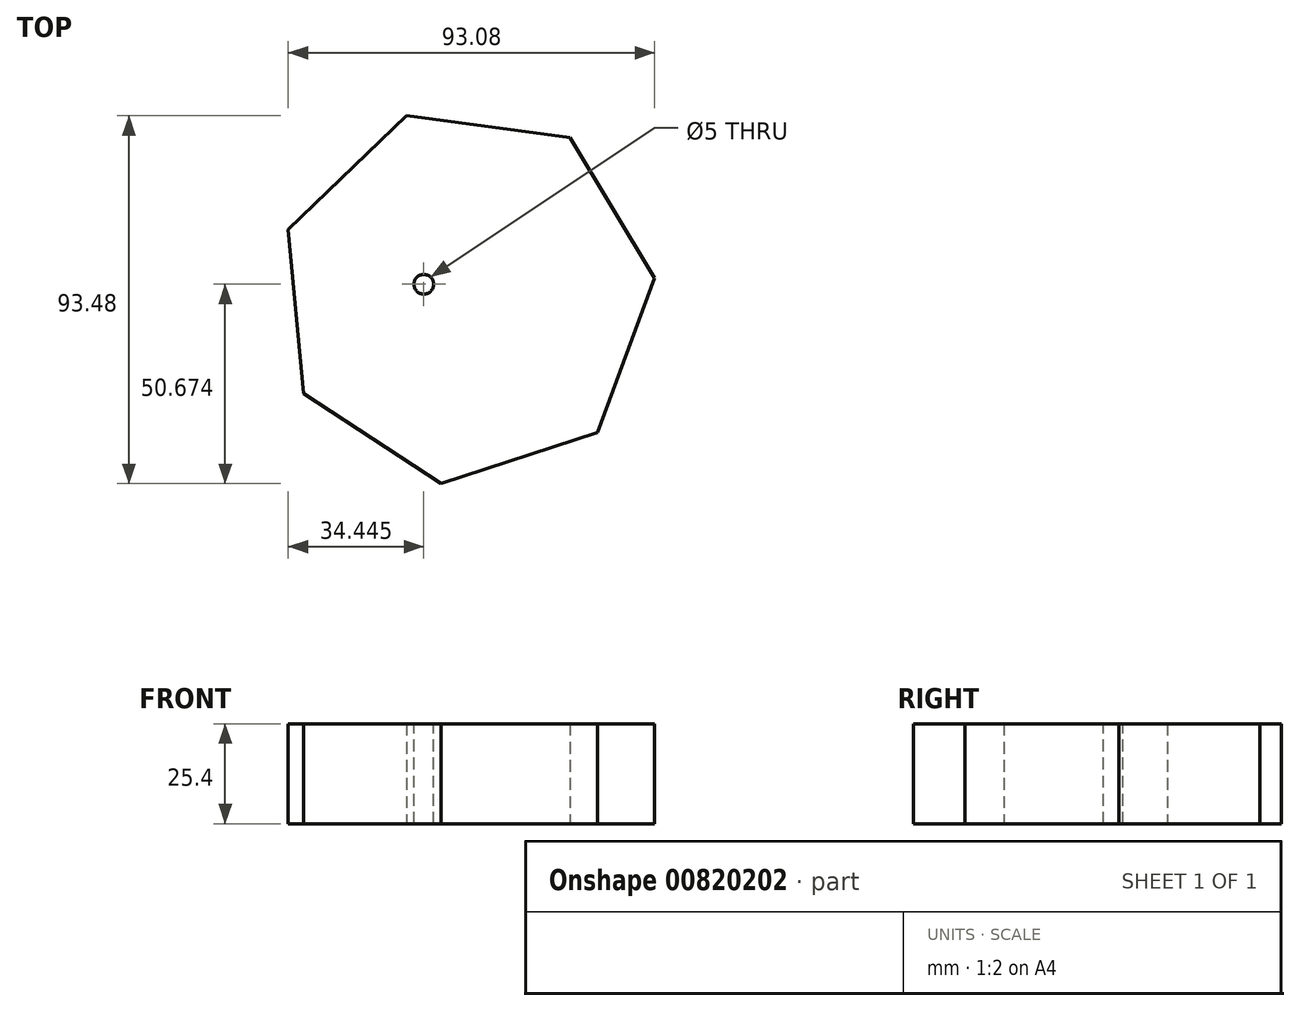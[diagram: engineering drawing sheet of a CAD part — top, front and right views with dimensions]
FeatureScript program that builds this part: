
annotation { "Feature Type Name" : "Feature", "Feature Type Description" : "" }
export const myFeature = defineFeature(function(context is Context, id is Id, definition is map)
    precondition{}
    {
        {
            var Q0;
            Q0=qCreatedBy(makeId("Top.planeOp"),FACE);
            var sketch = newSketch(context, id + "F0", { "sketchPlane" : qUnion([Q0])});
            skCircle(sketch, "E0.cCircle", {"center": v(15.97, -34.84) * mm, "radius": 43.38 * mm, "construction": true});
            skLineSegment(sketch, "E0.0", {"start": v(49.35, -69.54) * mm, "end": v(9.65, -82.57) * mm});
            skLineSegment(sketch, "E0.1", {"start": v(9.65, -82.57) * mm, "end": v(-25.29, -59.66) * mm});
            skLineSegment(sketch, "E0.2", {"start": v(-25.29, -59.66) * mm, "end": v(-29.16, -18.05) * mm});
            skLineSegment(sketch, "E0.3", {"start": v(-29.16, -18.05) * mm, "end": v(0.96, 10.91) * mm});
            skLineSegment(sketch, "E0.4", {"start": v(0.96, 10.91) * mm, "end": v(42.38, 5.43) * mm});
            skLineSegment(sketch, "E0.5", {"start": v(42.38, 5.43) * mm, "end": v(63.92, -30.38) * mm});
            skLineSegment(sketch, "E0.6", {"start": v(63.92, -30.38) * mm, "end": v(49.35, -69.54) * mm});
            skPoint(sketch, "E0.0.midPoint", {"position": v(29.5, -76.06) * mm});
            skSolve(sketch);
        }
        {
            var Q0;
            Q0=makeQuery(id+"F0.imprint","IMPRINT",FACE,{"disambiguationData":[TD([[makeQuery(id+"F0.imprint","IMPRINT",EDGE,{"derivedFrom":sQuery(id+"F0.wireOp",EDGE,"E0.0")}),-1.0]])]});
            extrude(context, id + "F1", {"entities" : qUnion([Q0]), "depth" : 25.4 * mm, "offsetDistance" : 25.4 * mm});
        }
        {
            var Q0;
            Q0=makeQuery(id+"F1.opExtrude","CAP_FACE",FACE,{"disambiguationData":[OSD([sQuery(id+"F0.wireOp",EDGE,"E0.0"),sQuery(id+"F0.wireOp",EDGE,"E0.1"),sQuery(id+"F0.wireOp",EDGE,"E0.2"),sQuery(id+"F0.wireOp",EDGE,"E0.3"),sQuery(id+"F0.wireOp",EDGE,"E0.4"),sQuery(id+"F0.wireOp",EDGE,"E0.5"),sQuery(id+"F0.wireOp",EDGE,"E0.6")])],"isStart":false});
            var sketch = newSketch(context, id + "F2", { "sketchPlane" : qUnion([Q0])});
            skPoint(sketch, "E1", {"position": v(5.29, -31.9) * mm});
            skSolve(sketch);
        }
        {
            var Q0;
            Q0=sQuery(id+"F2.wireOp",VERTEX,"E1");
            var Q1;
            Q1=makeQuery(id+"F1.opExtrude","SWEPT_BODY",BODY,{"disambiguationData":[OSD([sQuery(id+"F0.wireOp",EDGE,"E0.0"),sQuery(id+"F0.wireOp",EDGE,"E0.1"),sQuery(id+"F0.wireOp",EDGE,"E0.2"),sQuery(id+"F0.wireOp",EDGE,"E0.3"),sQuery(id+"F0.wireOp",EDGE,"E0.4"),sQuery(id+"F0.wireOp",EDGE,"E0.5"),sQuery(id+"F0.wireOp",EDGE,"E0.6")])]});
            hole(context, id + "F3", {"style" : HoleStyle.SIMPLE, "endStyle" : HoleEndStyle.THROUGH, "standardTappedOrClearance" : lookupTablePath({ "standard" : "ISO", "size" : "5", "type" : "Drilled" }), "standardBlindInLast" : lookupTablePath({ "standard" : "ISO", "size" : "5", "type" : "Drilled" }), "holeDiameter" : 5 * mm, "majorDiameter" : 6.35 * mm, "isTappedThrough" : true, "tappedDepth" : 12.7 * mm, "tapClearance" : 3, "locations" : qUnion([Q0]), "scope" : qUnion([Q1])});
        }
    });
